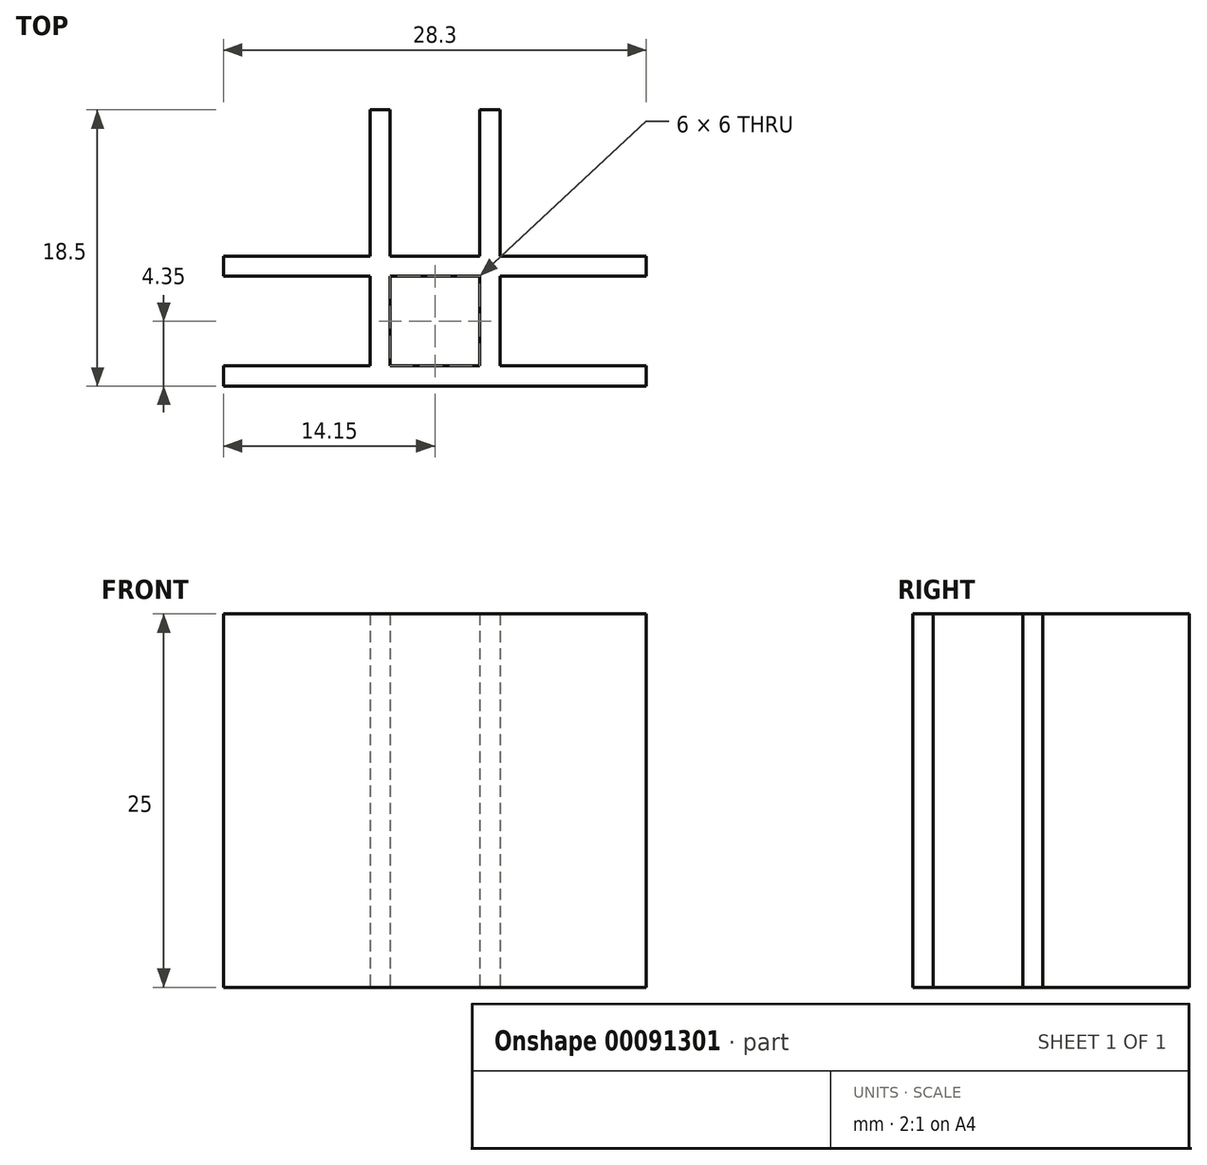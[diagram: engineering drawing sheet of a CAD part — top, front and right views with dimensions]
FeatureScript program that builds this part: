
annotation { "Feature Type Name" : "Feature", "Feature Type Description" : "" }
export const myFeature = defineFeature(function(context is Context, id is Id, definition is map)
    precondition{}
    {
        {
            var Q0;
            Q0=qCreatedBy(makeId("Top.planeOp"),FACE);
            var sketch = newSketch(context, id + "F0", { "sketchPlane" : qUnion([Q0])});
            skLineSegment(sketch, "E0.bottom", {"start": v(3, -3) * mm, "end": v(-3, -3) * mm});
            skLineSegment(sketch, "E0.top", {"start": v(3, 3) * mm, "end": v(-3, 3) * mm});
            skLineSegment(sketch, "E0.left", {"start": v(3, -3) * mm, "end": v(3, 3) * mm});
            skLineSegment(sketch, "E0.right", {"start": v(-3, -3) * mm, "end": v(-3, 3) * mm});
            skPoint(sketch, "E0.middle", {"position": v(0, 0) * mm});
            skLineSegment(sketch, "E1.0", {"start": v(4.35, 4.35) * mm, "end": v(-4.35, 4.35) * mm});
            skLineSegment(sketch, "E1.1", {"start": v(4.35, -4.35) * mm, "end": v(4.35, 4.35) * mm});
            skLineSegment(sketch, "E1.2", {"start": v(4.35, -4.35) * mm, "end": v(-4.35, -4.35) * mm});
            skLineSegment(sketch, "E1.3", {"start": v(-4.35, -4.35) * mm, "end": v(-4.35, 4.35) * mm});
            skLineSegment(sketch, "E2", {"start": v(-3, 3) * mm, "end": v(-3, 14.15) * mm});
            skLineSegment(sketch, "E3", {"start": v(-3, 14.15) * mm, "end": v(-4.35, 14.15) * mm});
            skLineSegment(sketch, "E4", {"start": v(-4.35, 14.15) * mm, "end": v(-4.35, 4.35) * mm});
            skLineSegment(sketch, "E5", {"start": v(-4.35, 4.35) * mm, "end": v(-14.15, 4.35) * mm});
            skLineSegment(sketch, "E6", {"start": v(-14.15, 4.35) * mm, "end": v(-14.15, 3) * mm});
            skLineSegment(sketch, "E7", {"start": v(-14.15, 3) * mm, "end": v(-3, 3) * mm});
            skLineSegment(sketch, "E8", {"start": v(-3, -3) * mm, "end": v(-14.15, -3) * mm});
            skLineSegment(sketch, "E9", {"start": v(-14.15, -3) * mm, "end": v(-14.15, -4.35) * mm});
            skLineSegment(sketch, "E10", {"start": v(-14.15, -4.35) * mm, "end": v(-4.35, -4.35) * mm});
            skLineSegment(sketch, "E11", {"start": v(0, 16.6) * mm, "end": v(0, -14.15) * mm, "construction": true});
            skPoint(sketch, "E11.startSnap0", {"position": v(0, 3) * mm});
            skLineSegment(sketch, "E12.MirrorCS", {"start": v(14.15, -3) * mm, "end": v(14.15, -4.35) * mm});
            skLineSegment(sketch, "E13.MirrorCS", {"start": v(14.15, 4.35) * mm, "end": v(14.15, 3) * mm});
            skLineSegment(sketch, "E14.MirrorCS", {"start": v(3, 14.15) * mm, "end": v(4.35, 14.15) * mm});
            skLineSegment(sketch, "E15.MirrorCS", {"start": v(3, -3) * mm, "end": v(14.15, -3) * mm});
            skLineSegment(sketch, "E16.MirrorCS", {"start": v(4.35, 4.35) * mm, "end": v(14.15, 4.35) * mm});
            skLineSegment(sketch, "E17.MirrorCS", {"start": v(14.15, -4.35) * mm, "end": v(4.35, -4.35) * mm});
            skLineSegment(sketch, "E18.MirrorCS", {"start": v(3, 3) * mm, "end": v(3, 14.15) * mm});
            skLineSegment(sketch, "E19.MirrorCS", {"start": v(4.35, 14.15) * mm, "end": v(4.35, 4.35) * mm});
            skLineSegment(sketch, "E20.MirrorCS", {"start": v(14.15, 3) * mm, "end": v(3, 3) * mm});
            skSolve(sketch);
        }
        {
            var Q0;
            Q0 = qSketchRegion(id + "F0", true);
            extrude(context, id + "F1", {"entities" : qUnion([Q0]), "depth" : 25 * mm, "offsetDistance" : 25 * mm});
        }
    });
